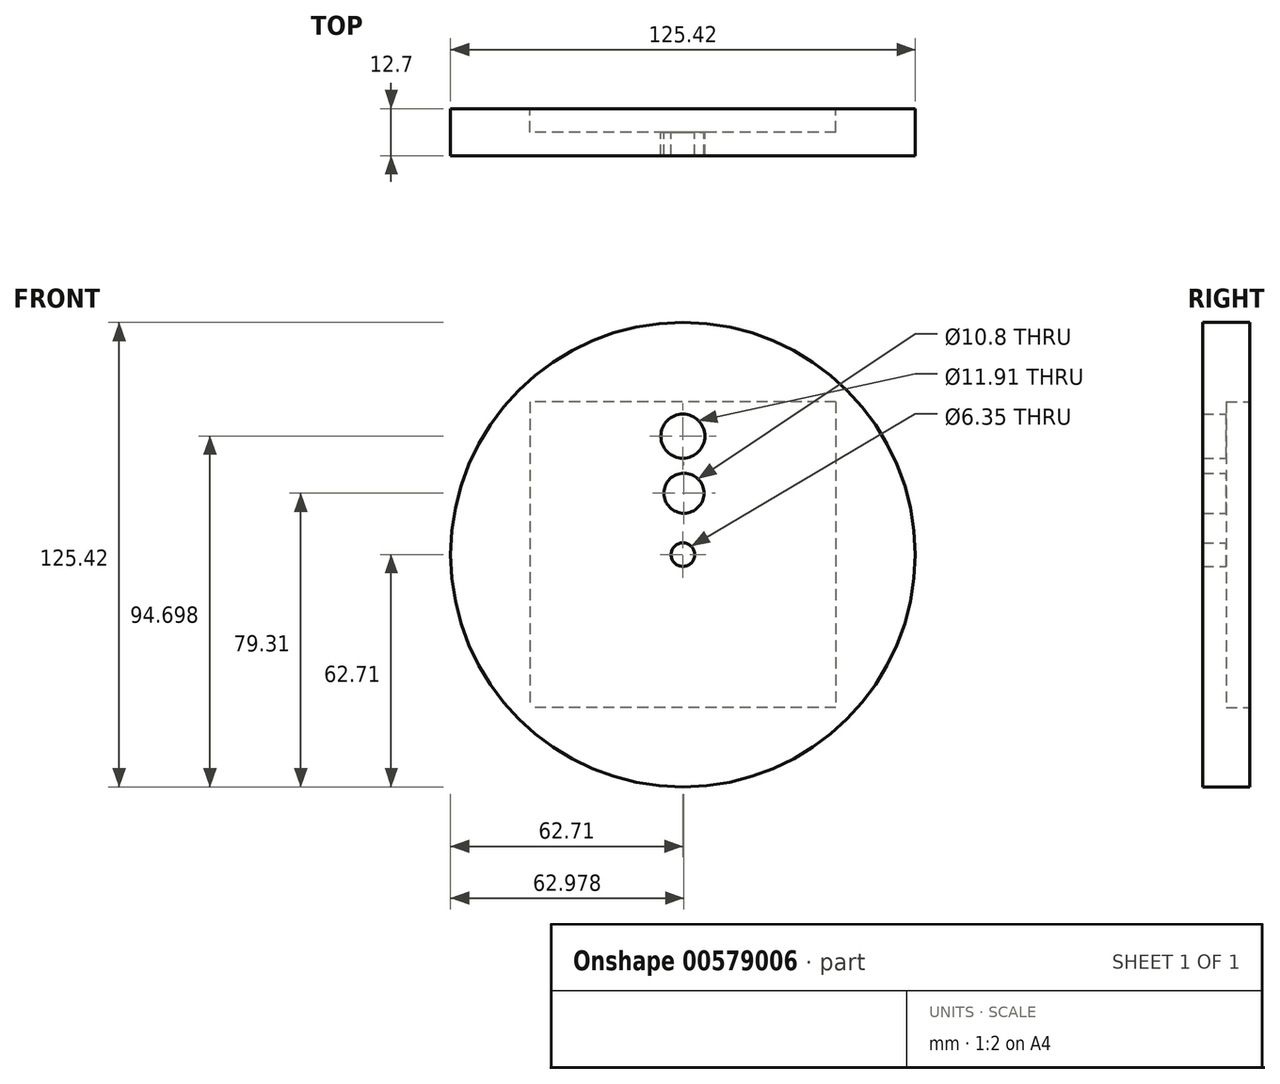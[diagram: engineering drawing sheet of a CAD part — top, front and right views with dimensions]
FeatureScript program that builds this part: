
annotation { "Feature Type Name" : "Feature", "Feature Type Description" : "" }
export const myFeature = defineFeature(function(context is Context, id is Id, definition is map)
    precondition{}
    {
        {
            var Q0;
            Q0=qCreatedBy(makeId("Front.planeOp"),FACE);
            var sketch = newSketch(context, id + "F0", { "sketchPlane" : qUnion([Q0])});
            skCircle(sketch, "E0", {"center": v(0, 0) * mm, "radius": 62.7 * mm});
            skLineSegment(sketch, "E1.bottom", {"start": v(41.28, 41.28) * mm, "end": v(-41.27, 41.28) * mm});
            skLineSegment(sketch, "E1.top", {"start": v(41.27, -41.27) * mm, "end": v(-41.28, -41.27) * mm});
            skLineSegment(sketch, "E1.left", {"start": v(41.28, 41.28) * mm, "end": v(41.27, -41.27) * mm});
            skLineSegment(sketch, "E1.right", {"start": v(-41.27, 41.28) * mm, "end": v(-41.28, -41.27) * mm});
            skCircle(sketch, "E2", {"center": v(0, 0) * mm, "radius": 3.18 * mm});
            skPoint(sketch, "E3.startSnap0", {"position": v(0, 41.28) * mm});
            skCircle(sketch, "E4", {"center": v(0.27, 16.6) * mm, "radius": 5.4 * mm});
            skCircle(sketch, "E5", {"center": v(0, 31.99) * mm, "radius": 5.95 * mm});
            skSolve(sketch);
        }
        {
            var Q0;
            Q0=makeQuery(id+"F0.imprint","IMPRINT",FACE,{"disambiguationData":[TD([[makeQuery(id+"F0.imprint","IMPRINT",EDGE,{"derivedFrom":sQuery(id+"F0.wireOp",EDGE,"E0")}),1.0]])]});
            extrude(context, id + "F1", {"entities" : qUnion([Q0]), "depth" : 12.7 * mm, "offsetDistance" : 25.4 * mm});
        }
        {
            var Q0;
            Q0=makeQuery(id+"F0.imprint","IMPRINT",FACE,{"disambiguationData":[TD([[makeQuery(id+"F0.imprint","IMPRINT",EDGE,{"derivedFrom":sQuery(id+"F0.wireOp",EDGE,"E1.bottom")}),1.0]])]});
            extrude(context, id + "F2", {"entities" : qUnion([Q0]), "operationType" : NewBodyOperationType.ADD, "depth" : 12.7 * mm, "offsetDistance" : 25.4 * mm});
        }
        {
            var Q0;
            Q0=makeQuery(id+"F0.imprint","IMPRINT",FACE,{"disambiguationData":[TD([[makeQuery(id+"F0.imprint","IMPRINT",EDGE,{"derivedFrom":sQuery(id+"F0.wireOp",EDGE,"E1.bottom")}),1.0]])]});
            extrude(context, id + "F3", {"entities" : qUnion([Q0]), "operationType" : NewBodyOperationType.REMOVE, "depth" : 6.35 * mm, "offsetDistance" : 25.4 * mm});
        }
    });
